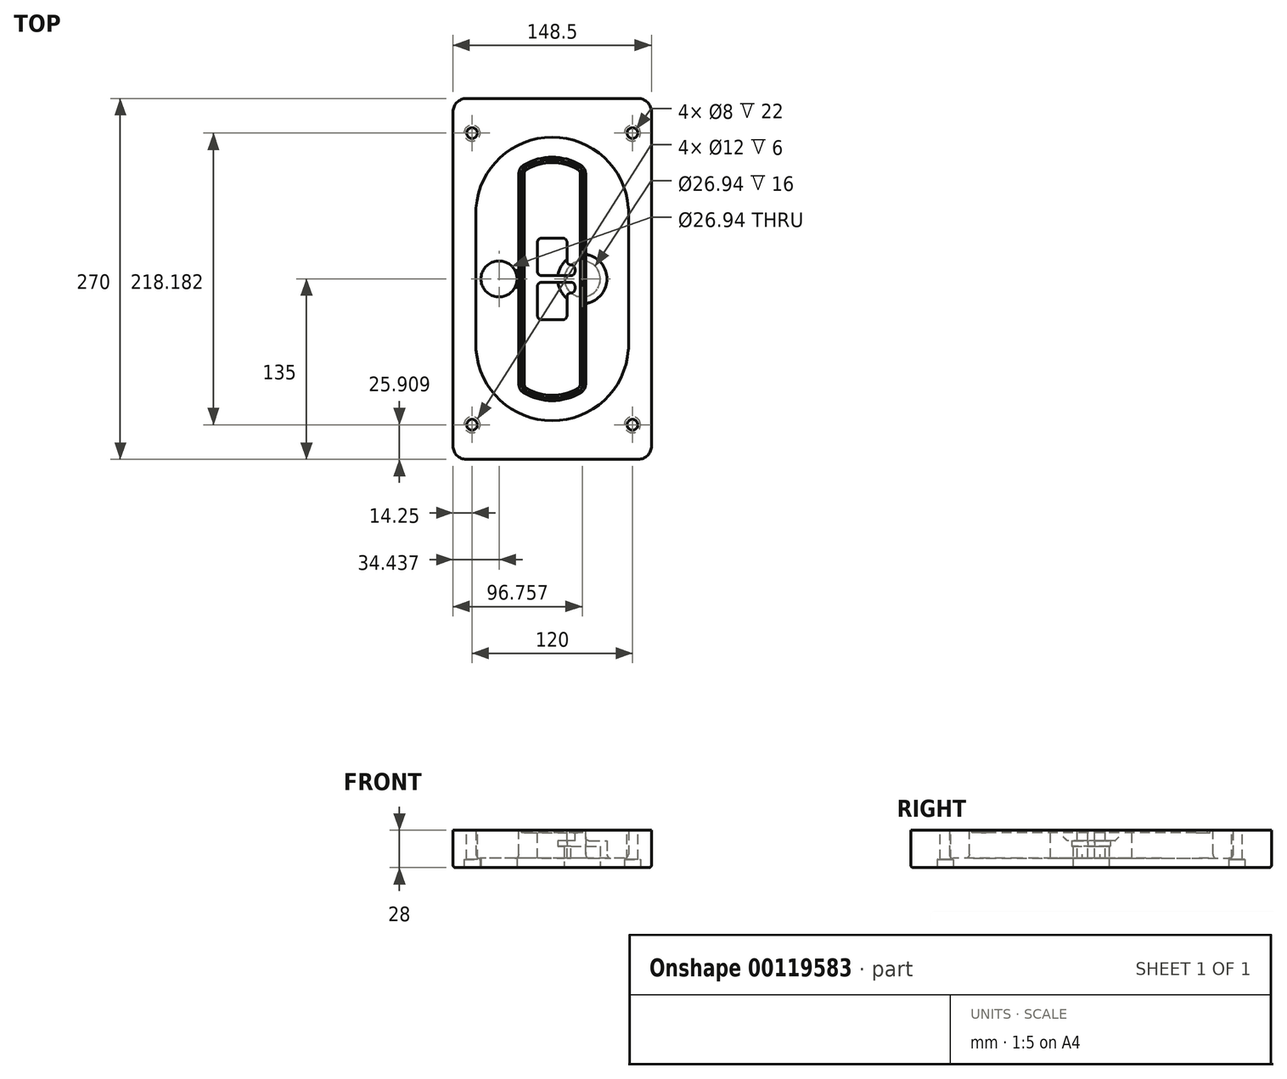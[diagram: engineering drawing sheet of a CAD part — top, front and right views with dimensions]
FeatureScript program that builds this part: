
annotation { "Feature Type Name" : "Feature", "Feature Type Description" : "" }
export const myFeature = defineFeature(function(context is Context, id is Id, definition is map)
    precondition{}
    {
        {
            var Q0;
            Q0=qCreatedBy(makeId("Top.planeOp"),FACE);
            var sketch = newSketch(context, id + "F0", { "sketchPlane" : qUnion([Q0])});
            skPoint(sketch, "E0.rect.middle", {"position": v(0, 0) * mm});
            skLineSegment(sketch, "E1.bottom", {"start": v(-64.25, -135) * mm, "end": v(64.25, -135) * mm});
            skLineSegment(sketch, "E1.top", {"start": v(-64.25, 135) * mm, "end": v(64.25, 135) * mm});
            skLineSegment(sketch, "E1.left", {"start": v(-74.25, -125) * mm, "end": v(-74.25, 125) * mm});
            skLineSegment(sketch, "E1.right", {"start": v(74.25, -125) * mm, "end": v(74.25, 125) * mm});
            skLineSegment(sketch, "E2", {"start": v(-74.25, 135) * mm, "end": v(74.25, -135) * mm, "construction": true});
            skLineSegment(sketch, "E3", {"start": v(74.25, 135) * mm, "end": v(-74.25, -135) * mm, "construction": true});
            skCircle(sketch, "E4", {"center": v(-60, 109.1) * mm, "radius": 4 * mm});
            skCircle(sketch, "E5", {"center": v(60, 109.1) * mm, "radius": 4 * mm});
            skCircle(sketch, "E6", {"center": v(60, -109.1) * mm, "radius": 4 * mm});
            skCircle(sketch, "E7", {"center": v(-60, -109.1) * mm, "radius": 4 * mm});
            skLineSegment(sketch, "E8", {"start": v(-60, 109.1) * mm, "end": v(60, 109.1) * mm, "construction": true});
            skLineSegment(sketch, "E9", {"start": v(60, 109.1) * mm, "end": v(60, -109.1) * mm, "construction": true});
            skLineSegment(sketch, "E10", {"start": v(60, -109.1) * mm, "end": v(-60, -109.1) * mm, "construction": true});
            skLineSegment(sketch, "E11", {"start": v(-60, -109.1) * mm, "end": v(-60, 109.1) * mm, "construction": true});
            skLineSegment(sketch, "E12", {"start": v(-60, 52.58) * mm, "end": v(-60, -52.58) * mm});
            skLineSegment(sketch, "E13", {"start": v(60, 52.58) * mm, "end": v(60, -52.58) * mm});
            skArc(sketch, "E14", {"start": v(59.97, 53.3) * mm, "mid": v(0, 109.1) * mm, "end": v(-59.97, 53.3) * mm});
            skArc(sketch, "E15", {"start": v(-59.97, -53.3) * mm, "mid": v(0, -109.1) * mm, "end": v(59.97, -53.3) * mm});
            skLineSegment(sketch, "E16", {"start": v(-60, 0) * mm, "end": v(60, 0) * mm, "construction": true});
            skPoint(sketch, "E17.visualSharp", {"position": v(-60, -45) * mm});
            skArc(sketch, "E17.filletArc", {"start": v(-60, -52.58) * mm, "mid": v(-60, -52.94) * mm, "end": v(-59.97, -53.3) * mm});
            skPoint(sketch, "E18.visualSharp", {"position": v(-60, 45) * mm});
            skArc(sketch, "E18.filletArc", {"start": v(-59.97, 53.3) * mm, "mid": v(-60, 52.94) * mm, "end": v(-60, 52.58) * mm});
            skPoint(sketch, "E19.visualSharp", {"position": v(60, 45) * mm});
            skArc(sketch, "E19.filletArc", {"start": v(60, 52.58) * mm, "mid": v(60, 52.94) * mm, "end": v(59.97, 53.3) * mm});
            skPoint(sketch, "E20.visualSharp", {"position": v(60, -45) * mm});
            skArc(sketch, "E20.filletArc", {"start": v(59.97, -53.3) * mm, "mid": v(60, -52.94) * mm, "end": v(60, -52.58) * mm});
            skPoint(sketch, "E21.visualSharp", {"position": v(-74.25, 135) * mm});
            skArc(sketch, "E21.filletArc", {"start": v(-64.25, 135) * mm, "mid": v(-71.32, 132.07) * mm, "end": v(-74.25, 125) * mm});
            skPoint(sketch, "E22.visualSharp", {"position": v(74.25, 135) * mm});
            skArc(sketch, "E22.filletArc", {"start": v(74.25, 125) * mm, "mid": v(71.32, 132.07) * mm, "end": v(64.25, 135) * mm});
            skPoint(sketch, "E23.visualSharp", {"position": v(74.25, -135) * mm});
            skArc(sketch, "E23.filletArc", {"start": v(64.25, -135) * mm, "mid": v(71.32, -132.07) * mm, "end": v(74.25, -125) * mm});
            skPoint(sketch, "E24.visualSharp", {"position": v(-74.25, -135) * mm});
            skArc(sketch, "E24.filletArc", {"start": v(-74.25, -125) * mm, "mid": v(-71.32, -132.07) * mm, "end": v(-64.25, -135) * mm});
            skArc(sketch, "E25.0", {"start": v(57, 52.58) * mm, "mid": v(57, 52.83) * mm, "end": v(56.98, 53.08) * mm});
            skLineSegment(sketch, "E25.1", {"start": v(57, 52.58) * mm, "end": v(57, -52.58) * mm});
            skArc(sketch, "E25.2", {"start": v(56.98, -53.08) * mm, "mid": v(57, -52.83) * mm, "end": v(57, -52.58) * mm});
            skArc(sketch, "E25.3", {"start": v(-56.98, -53.08) * mm, "mid": v(0, -106.1) * mm, "end": v(56.98, -53.08) * mm});
            skArc(sketch, "E25.4", {"start": v(-57, -52.58) * mm, "mid": v(-57, -52.83) * mm, "end": v(-56.98, -53.08) * mm});
            skArc(sketch, "E25.5", {"start": v(56.98, 53.08) * mm, "mid": v(0, 106.1) * mm, "end": v(-56.98, 53.08) * mm});
            skLineSegment(sketch, "E25.6", {"start": v(-57, 52.58) * mm, "end": v(-57, -52.58) * mm});
            skArc(sketch, "E25.7", {"start": v(-56.98, 53.08) * mm, "mid": v(-57, 52.83) * mm, "end": v(-57, 52.58) * mm});
            skArc(sketch, "E26.0", {"start": v(-63.96, 53.59) * mm, "mid": v(-64, 53.08) * mm, "end": v(-64, 52.58) * mm});
            skArc(sketch, "E26.1", {"start": v(63.96, 53.59) * mm, "mid": v(0, 113.1) * mm, "end": v(-63.96, 53.59) * mm});
            skArc(sketch, "E26.2", {"start": v(64, 52.58) * mm, "mid": v(64, 53.08) * mm, "end": v(63.96, 53.59) * mm});
            skLineSegment(sketch, "E26.3", {"start": v(64, 52.58) * mm, "end": v(64, -52.58) * mm});
            skArc(sketch, "E26.4", {"start": v(63.96, -53.59) * mm, "mid": v(64, -53.08) * mm, "end": v(64, -52.58) * mm});
            skLineSegment(sketch, "E26.5", {"start": v(-64, 52.58) * mm, "end": v(-64, -52.58) * mm});
            skArc(sketch, "E26.6", {"start": v(-63.96, -53.59) * mm, "mid": v(0, -113.1) * mm, "end": v(63.96, -53.59) * mm});
            skArc(sketch, "E26.7", {"start": v(-64, -52.58) * mm, "mid": v(-64, -53.08) * mm, "end": v(-63.96, -53.59) * mm});
            skSolve(sketch);
        }
        {
            var Q0;
            Q0=makeQuery(id+"F0.imprint","IMPRINT",FACE,{"disambiguationData":[TD([[makeQuery(id+"F0.imprint","IMPRINT",EDGE,{"derivedFrom":sQuery(id+"F0.wireOp",EDGE,"E1.bottom")}),1.0]])]});
            var Q1;
            Q1=makeQuery(id+"F0.imprint","IMPRINT",FACE,{"disambiguationData":[TD([[makeQuery(id+"F0.imprint","IMPRINT",EDGE,{"derivedFrom":sQuery(id+"F0.wireOp",EDGE,"E12")}),1.0]])]});
            var Q2;
            Q2=makeQuery(id+"F0.imprint","IMPRINT",FACE,{"disambiguationData":[TD([[makeQuery(id+"F0.imprint","IMPRINT",EDGE,{"derivedFrom":sQuery(id+"F0.wireOp",EDGE,"E25.0")}),1.0]])]});
            var Q3;
            Q3=makeQuery(id+"F0.imprint","IMPRINT",FACE,{"disambiguationData":[TD([[makeQuery(id+"F0.imprint","IMPRINT",EDGE,{"derivedFrom":sQuery(id+"F0.wireOp",EDGE,"E12")}),-1.0]])]});
            extrude(context, id + "F1", {"entities" : qUnion([Q0, Q1, Q2, Q3]), "oppositeDirection" : true, "depth" : 25 * mm});
        }
        {
            var Q0;
            Q0=makeQuery(id+"F0.imprint","IMPRINT",FACE,{"disambiguationData":[TD([[makeQuery(id+"F0.imprint","IMPRINT",EDGE,{"derivedFrom":sQuery(id+"F0.wireOp",EDGE,"E12")}),1.0]])]});
            extrude(context, id + "F2", {"entities" : qUnion([Q0]), "operationType" : NewBodyOperationType.ADD, "depth" : 3 * mm});
        }
        {
            var Q0;
            Q0=makeQuery(id+"F0.imprint","IMPRINT",FACE,{"disambiguationData":[TD([[makeQuery(id+"F0.imprint","IMPRINT",EDGE,{"derivedFrom":sQuery(id+"F0.wireOp",EDGE,"E25.0")}),1.0]])]});
            extrude(context, id + "F3", {"entities" : qUnion([Q0]), "operationType" : NewBodyOperationType.REMOVE, "oppositeDirection" : true, "depth" : 18 * mm});
        }
        {
            var Q0;
            Q0=makeQuery(id+"F2.opExtrude","CAP_FACE",FACE,{"disambiguationData":[OSD([sQuery(id+"F0.wireOp",EDGE,"E12"),sQuery(id+"F0.wireOp",EDGE,"E13"),sQuery(id+"F0.wireOp",EDGE,"E14"),sQuery(id+"F0.wireOp",EDGE,"E15"),sQuery(id+"F0.wireOp",EDGE,"E17.filletArc"),sQuery(id+"F0.wireOp",EDGE,"E18.filletArc"),sQuery(id+"F0.wireOp",EDGE,"E19.filletArc"),sQuery(id+"F0.wireOp",EDGE,"E20.filletArc"),sQuery(id+"F0.wireOp",EDGE,"E25.0"),sQuery(id+"F0.wireOp",EDGE,"E25.1"),sQuery(id+"F0.wireOp",EDGE,"E25.2"),sQuery(id+"F0.wireOp",EDGE,"E25.3"),sQuery(id+"F0.wireOp",EDGE,"E25.4"),sQuery(id+"F0.wireOp",EDGE,"E25.5"),sQuery(id+"F0.wireOp",EDGE,"E25.6"),sQuery(id+"F0.wireOp",EDGE,"E25.7")])],"isStart":false});
            var sketch = newSketch(context, id + "F4", { "sketchPlane" : qUnion([Q0])});
            skArc(sketch, "E27.0", {"start": v(-20.98, -85.5) * mm, "mid": v(0, -91.1) * mm, "end": v(20.98, -85.5) * mm});
            skArc(sketch, "E28.0", {"start": v(20.98, 85.5) * mm, "mid": v(0, 91.1) * mm, "end": v(-20.98, 85.5) * mm});
            skLineSegment(sketch, "E29", {"start": v(-25, 78.56) * mm, "end": v(-25, -78.56) * mm});
            skLineSegment(sketch, "E30", {"start": v(25, 78.56) * mm, "end": v(25, -78.56) * mm});
            skLineSegment(sketch, "E31", {"start": v(-25, 82.87) * mm, "end": v(25, 82.87) * mm, "construction": true});
            skLineSegment(sketch, "E32", {"start": v(-25, -82.87) * mm, "end": v(25, -82.87) * mm, "construction": true});
            skPoint(sketch, "E33.visualSharp", {"position": v(-25, 82.87) * mm});
            skArc(sketch, "E33.filletArc", {"start": v(-20.98, 85.5) * mm, "mid": v(-23.92, 82.56) * mm, "end": v(-25, 78.56) * mm});
            skPoint(sketch, "E34.visualSharp", {"position": v(25, 82.87) * mm});
            skArc(sketch, "E34.filletArc", {"start": v(25, 78.56) * mm, "mid": v(23.92, 82.56) * mm, "end": v(20.98, 85.5) * mm});
            skPoint(sketch, "E35.visualSharp", {"position": v(25, -82.87) * mm});
            skArc(sketch, "E35.filletArc", {"start": v(20.98, -85.5) * mm, "mid": v(23.92, -82.56) * mm, "end": v(25, -78.56) * mm});
            skPoint(sketch, "E36.visualSharp", {"position": v(-25, -82.87) * mm});
            skArc(sketch, "E36.filletArc", {"start": v(-25, -78.56) * mm, "mid": v(-23.92, -82.56) * mm, "end": v(-20.98, -85.5) * mm});
            skArc(sketch, "E37.0", {"start": v(56.98, 53.08) * mm, "mid": v(0, 106.1) * mm, "end": v(-56.98, 53.08) * mm});
            skArc(sketch, "E37.1", {"start": v(-56.98, 53.08) * mm, "mid": v(-57, 52.83) * mm, "end": v(-57, 52.58) * mm});
            skLineSegment(sketch, "E37.2", {"start": v(-57, 52.58) * mm, "end": v(-57, -52.58) * mm});
            skArc(sketch, "E37.3", {"start": v(-57, -52.58) * mm, "mid": v(-57, -52.83) * mm, "end": v(-56.98, -53.08) * mm});
            skArc(sketch, "E37.4", {"start": v(-56.98, -53.08) * mm, "mid": v(0, -106.1) * mm, "end": v(56.98, -53.08) * mm});
            skArc(sketch, "E37.5", {"start": v(56.98, -53.08) * mm, "mid": v(57, -52.83) * mm, "end": v(57, -52.58) * mm});
            skLineSegment(sketch, "E37.6", {"start": v(57, 52.58) * mm, "end": v(57, -52.58) * mm});
            skArc(sketch, "E37.7", {"start": v(57, 52.58) * mm, "mid": v(57, 52.83) * mm, "end": v(56.98, 53.08) * mm});
            skLineSegment(sketch, "E38.0", {"start": v(23, 78.56) * mm, "end": v(23, -78.56) * mm});
            skArc(sketch, "E38.1", {"start": v(19.99, -83.76) * mm, "mid": v(22.2, -81.56) * mm, "end": v(23, -78.56) * mm});
            skArc(sketch, "E38.2", {"start": v(-19.99, -83.76) * mm, "mid": v(0, -89.1) * mm, "end": v(19.99, -83.76) * mm});
            skArc(sketch, "E38.3", {"start": v(-23, -78.56) * mm, "mid": v(-22.2, -81.56) * mm, "end": v(-19.99, -83.76) * mm});
            skLineSegment(sketch, "E38.4", {"start": v(-23, 78.56) * mm, "end": v(-23, -78.56) * mm});
            skArc(sketch, "E38.5", {"start": v(23, 78.56) * mm, "mid": v(22.2, 81.56) * mm, "end": v(19.99, 83.76) * mm});
            skArc(sketch, "E38.6", {"start": v(-19.99, 83.76) * mm, "mid": v(-22.2, 81.56) * mm, "end": v(-23, 78.56) * mm});
            skArc(sketch, "E38.7", {"start": v(19.99, 83.76) * mm, "mid": v(0, 89.1) * mm, "end": v(-19.99, 83.76) * mm});
            skArc(sketch, "E39.0", {"start": v(21, 78.56) * mm, "mid": v(20.46, 80.56) * mm, "end": v(19, 82.02) * mm});
            skLineSegment(sketch, "E39.1", {"start": v(21, 78.56) * mm, "end": v(21, -78.56) * mm});
            skArc(sketch, "E39.2", {"start": v(19, -82.02) * mm, "mid": v(20.46, -80.56) * mm, "end": v(21, -78.56) * mm});
            skArc(sketch, "E39.3", {"start": v(-19, -82.02) * mm, "mid": v(0, -87.1) * mm, "end": v(19, -82.02) * mm});
            skArc(sketch, "E39.4", {"start": v(-21, -78.56) * mm, "mid": v(-20.46, -80.56) * mm, "end": v(-19, -82.02) * mm});
            skArc(sketch, "E39.5", {"start": v(19, 82.02) * mm, "mid": v(0, 87.1) * mm, "end": v(-19, 82.02) * mm});
            skLineSegment(sketch, "E39.6", {"start": v(-21, 78.56) * mm, "end": v(-21, -78.56) * mm});
            skArc(sketch, "E39.7", {"start": v(-19, 82.02) * mm, "mid": v(-20.46, 80.56) * mm, "end": v(-21, 78.56) * mm});
            skLineSegment(sketch, "E40", {"start": v(-25, 0) * mm, "end": v(25, 0) * mm, "construction": true});
            skLineSegment(sketch, "E41", {"start": v(-11, 5.5) * mm, "end": v(-11, 27.5) * mm});
            skLineSegment(sketch, "E42", {"start": v(-8, 30.5) * mm, "end": v(8, 30.5) * mm});
            skLineSegment(sketch, "E43", {"start": v(11, 27.5) * mm, "end": v(11, 13.5) * mm});
            skLineSegment(sketch, "E44", {"start": v(14, 10.5) * mm, "end": v(14, 10.5) * mm});
            skLineSegment(sketch, "E45", {"start": v(17, 7.5) * mm, "end": v(17, 5.5) * mm});
            skLineSegment(sketch, "E46", {"start": v(14, 2.5) * mm, "end": v(-8, 2.5) * mm});
            skPoint(sketch, "E47.visualSharp", {"position": v(-11, 30.5) * mm});
            skArc(sketch, "E47.filletArc", {"start": v(-8, 30.5) * mm, "mid": v(-10.12, 29.62) * mm, "end": v(-11, 27.5) * mm});
            skPoint(sketch, "E48.visualSharp", {"position": v(11, 30.5) * mm});
            skArc(sketch, "E48.filletArc", {"start": v(11, 27.5) * mm, "mid": v(10.12, 29.62) * mm, "end": v(8, 30.5) * mm});
            skPoint(sketch, "E49.visualSharp", {"position": v(11, 10.5) * mm});
            skArc(sketch, "E49.filletArc", {"start": v(11, 13.5) * mm, "mid": v(11.88, 11.38) * mm, "end": v(14, 10.5) * mm});
            skPoint(sketch, "E50.visualSharp", {"position": v(17, 10.5) * mm});
            skArc(sketch, "E50.filletArc", {"start": v(17, 7.5) * mm, "mid": v(16.12, 9.62) * mm, "end": v(14, 10.5) * mm});
            skPoint(sketch, "E51.visualSharp", {"position": v(17, 2.5) * mm});
            skArc(sketch, "E51.filletArc", {"start": v(14, 2.5) * mm, "mid": v(16.12, 3.38) * mm, "end": v(17, 5.5) * mm});
            skPoint(sketch, "E52.visualSharp", {"position": v(-11, 2.5) * mm});
            skArc(sketch, "E52.filletArc", {"start": v(-11, 5.5) * mm, "mid": v(-10.12, 3.38) * mm, "end": v(-8, 2.5) * mm});
            skLineSegment(sketch, "E53.0.MirrorCS", {"start": v(14, -2.5) * mm, "end": v(-8, -2.5) * mm});
            skArc(sketch, "E54.0.MirrorCS", {"start": v(-11, -5.5) * mm, "mid": v(-10.12, -3.38) * mm, "end": v(-8, -2.5) * mm});
            skLineSegment(sketch, "E55.0.MirrorCS", {"start": v(-11, -5.5) * mm, "end": v(-11, -27.5) * mm});
            skArc(sketch, "E56.0.MirrorCS", {"start": v(-8, -30.5) * mm, "mid": v(-10.12, -29.62) * mm, "end": v(-11, -27.5) * mm});
            skLineSegment(sketch, "E57.0.MirrorCS", {"start": v(-8, -30.5) * mm, "end": v(8, -30.5) * mm});
            skArc(sketch, "E58.0.MirrorCS", {"start": v(11, -27.5) * mm, "mid": v(10.12, -29.62) * mm, "end": v(8, -30.5) * mm});
            skLineSegment(sketch, "E59.0.MirrorCS", {"start": v(11, -27.5) * mm, "end": v(11, -13.5) * mm});
            skArc(sketch, "E60.0.MirrorCS", {"start": v(11, -13.5) * mm, "mid": v(11.88, -11.38) * mm, "end": v(14, -10.5) * mm});
            skArc(sketch, "E61.0.MirrorCS", {"start": v(17, -7.5) * mm, "mid": v(16.12, -9.62) * mm, "end": v(14, -10.5) * mm});
            skLineSegment(sketch, "E62.0.MirrorCS", {"start": v(17, -7.5) * mm, "end": v(17, -5.5) * mm});
            skArc(sketch, "E63.0.MirrorCS", {"start": v(14, -2.5) * mm, "mid": v(16.12, -3.38) * mm, "end": v(17, -5.5) * mm});
            skSolve(sketch);
        }
        {
            var Q0;
            Q0=makeQuery(id+"F4.imprint","IMPRINT",FACE,{"disambiguationData":[TD([[makeQuery(id+"F4.imprint","IMPRINT",EDGE,{"derivedFrom":sQuery(id+"F4.wireOp",EDGE,"E27.0")}),1.0]])]});
            var Q1;
            Q1=makeQuery(id+"F4.imprint","IMPRINT",FACE,{"disambiguationData":[TD([[makeQuery(id+"F4.imprint","IMPRINT",EDGE,{"derivedFrom":sQuery(id+"F4.wireOp",EDGE,"E38.0")}),-1.0]])]});
            var Q2;
            Q2=makeQuery(id+"F4.imprint","IMPRINT",FACE,{"disambiguationData":[TD([[makeQuery(id+"F4.imprint","IMPRINT",EDGE,{"derivedFrom":sQuery(id+"F4.wireOp",EDGE,"E39.0")}),1.0]])]});
            extrude(context, id + "F5", {"entities" : qUnion([Q0, Q1, Q2]), "operationType" : NewBodyOperationType.ADD, "endBound" : BoundingType.UP_TO_NEXT, "oppositeDirection" : true, "depth" : 25 * mm});
        }
        {
            var Q0;
            Q0=makeQuery(id+"F4.imprint","IMPRINT",FACE,{"disambiguationData":[TD([[makeQuery(id+"F4.imprint","IMPRINT",EDGE,{"derivedFrom":sQuery(id+"F4.wireOp",EDGE,"E38.0")}),-1.0]])]});
            extrude(context, id + "F6", {"entities" : qUnion([Q0]), "operationType" : NewBodyOperationType.REMOVE, "oppositeDirection" : true, "depth" : 2 * mm});
        }
        {
            var Q0;
            Q0=makeQuery(id+"F1.opExtrude","CAP_FACE",FACE,{"disambiguationData":[OSD([sQuery(id+"F0.wireOp",EDGE,"E1.bottom"),sQuery(id+"F0.wireOp",EDGE,"E1.top"),sQuery(id+"F0.wireOp",EDGE,"E1.left"),sQuery(id+"F0.wireOp",EDGE,"E1.right"),sQuery(id+"F0.wireOp",EDGE,"E4"),sQuery(id+"F0.wireOp",EDGE,"E5"),sQuery(id+"F0.wireOp",EDGE,"E6"),sQuery(id+"F0.wireOp",EDGE,"E7"),sQuery(id+"F0.wireOp",EDGE,"E21.filletArc"),sQuery(id+"F0.wireOp",EDGE,"E22.filletArc"),sQuery(id+"F0.wireOp",EDGE,"E23.filletArc"),sQuery(id+"F0.wireOp",EDGE,"E24.filletArc")])],"isStart":false});
            var sketch = newSketch(context, id + "F7", { "sketchPlane" : qUnion([Q0])});
            skCircle(sketch, "E64", {"center": v(22.5, 0) * mm, "radius": 13.47 * mm});
            skCircle(sketch, "E65", {"center": v(-39.81, 0) * mm, "radius": 13.47 * mm});
            skLineSegment(sketch, "E66", {"start": v(74.25, 0) * mm, "end": v(-74.25, 0) * mm});
            skCircle(sketch, "E67", {"center": v(22.5, 0) * mm, "radius": 18.47 * mm});
            skCircle(sketch, "E68", {"center": v(60, -109.1) * mm, "radius": 6 * mm});
            skCircle(sketch, "E69", {"center": v(-60, -109.1) * mm, "radius": 6 * mm});
            skCircle(sketch, "E70", {"center": v(-60, 109.1) * mm, "radius": 6 * mm});
            skCircle(sketch, "E71", {"center": v(60, 109.1) * mm, "radius": 6 * mm});
            skSolve(sketch);
        }
        {
            var Q0;
            {var subQ1=sQuery(id+"F7.wireOp",EDGE,"E66");var subQ4=sQuery(id+"F7.wireOp",EDGE,"E64");var subQ6=makeQuery(id+"F7.imprint","INTERSECT",VERTEX,{"disambiguationData":[OD(0.0)],"derivedFrom":[subQ4,subQ1]});Q0=makeQuery(id+"F7.imprint","IMPRINT",FACE,{"disambiguationData":[TD([[makeQuery(id+"F7.imprint","IMPRINT",EDGE,{"disambiguationData":[TD([[subQ6,-1.0]])],"derivedFrom":subQ4}),-1.0]])]});}
            var Q1;
            {var subQ0=sQuery(id+"F7.wireOp",EDGE,"E66");var subQ1=sQuery(id+"F7.wireOp",EDGE,"E64");var subQ3=makeQuery(id+"F7.imprint","INTERSECT",VERTEX,{"disambiguationData":[OD(0.0)],"derivedFrom":[subQ1,subQ0]});Q1=makeQuery(id+"F7.imprint","IMPRINT",FACE,{"disambiguationData":[TD([[makeQuery(id+"F7.imprint","IMPRINT",EDGE,{"disambiguationData":[TD([[subQ3,-1.0]])],"derivedFrom":subQ1}),1.0]])]});}
            var Q2;
            {var subQ0=sQuery(id+"F7.wireOp",EDGE,"E66");var subQ1=sQuery(id+"F7.wireOp",EDGE,"E64");var subQ3=makeQuery(id+"F7.imprint","INTERSECT",VERTEX,{"disambiguationData":[OD(0.0)],"derivedFrom":[subQ1,subQ0]});Q2=makeQuery(id+"F7.imprint","IMPRINT",FACE,{"disambiguationData":[TD([[makeQuery(id+"F7.imprint","IMPRINT",EDGE,{"disambiguationData":[TD([[subQ3,1.0]])],"derivedFrom":subQ1}),1.0]])]});}
            var Q3;
            {var subQ1=sQuery(id+"F7.wireOp",EDGE,"E66");var subQ4=sQuery(id+"F7.wireOp",EDGE,"E64");var subQ6=makeQuery(id+"F7.imprint","INTERSECT",VERTEX,{"disambiguationData":[OD(0.0)],"derivedFrom":[subQ4,subQ1]});Q3=makeQuery(id+"F7.imprint","IMPRINT",FACE,{"disambiguationData":[TD([[makeQuery(id+"F7.imprint","IMPRINT",EDGE,{"disambiguationData":[TD([[subQ6,1.0]])],"derivedFrom":subQ4}),-1.0]])]});}
            extrude(context, id + "F8", {"entities" : qUnion([Q0, Q1, Q2, Q3]), "operationType" : NewBodyOperationType.ADD, "oppositeDirection" : true, "depth" : 20 * mm});
        }
        {
            var Q0;
            {var subQ0=sQuery(id+"F7.wireOp",EDGE,"E66");var subQ1=sQuery(id+"F7.wireOp",EDGE,"E64");var subQ3=makeQuery(id+"F7.imprint","INTERSECT",VERTEX,{"disambiguationData":[OD(0.0)],"derivedFrom":[subQ1,subQ0]});Q0=makeQuery(id+"F7.imprint","IMPRINT",FACE,{"disambiguationData":[TD([[makeQuery(id+"F7.imprint","IMPRINT",EDGE,{"disambiguationData":[TD([[subQ3,-1.0]])],"derivedFrom":subQ1}),1.0]])]});}
            var Q1;
            {var subQ0=sQuery(id+"F7.wireOp",EDGE,"E66");var subQ1=sQuery(id+"F7.wireOp",EDGE,"E64");var subQ3=makeQuery(id+"F7.imprint","INTERSECT",VERTEX,{"disambiguationData":[OD(0.0)],"derivedFrom":[subQ1,subQ0]});Q1=makeQuery(id+"F7.imprint","IMPRINT",FACE,{"disambiguationData":[TD([[makeQuery(id+"F7.imprint","IMPRINT",EDGE,{"disambiguationData":[TD([[subQ3,1.0]])],"derivedFrom":subQ1}),1.0]])]});}
            extrude(context, id + "F9", {"entities" : qUnion([Q0, Q1]), "operationType" : NewBodyOperationType.REMOVE, "oppositeDirection" : true, "depth" : 16 * mm});
        }
        {
            var Q0;
            {var subQ0=sQuery(id+"F7.wireOp",EDGE,"E66");var subQ1=sQuery(id+"F7.wireOp",EDGE,"E65");var subQ3=makeQuery(id+"F7.imprint","INTERSECT",VERTEX,{"disambiguationData":[OD(0.0)],"derivedFrom":[subQ1,subQ0]});Q0=makeQuery(id+"F7.imprint","IMPRINT",FACE,{"disambiguationData":[TD([[makeQuery(id+"F7.imprint","IMPRINT",EDGE,{"disambiguationData":[TD([[subQ3,-1.0]])],"derivedFrom":subQ1}),1.0]])]});}
            var Q1;
            {var subQ0=sQuery(id+"F7.wireOp",EDGE,"E66");var subQ1=sQuery(id+"F7.wireOp",EDGE,"E65");var subQ3=makeQuery(id+"F7.imprint","INTERSECT",VERTEX,{"disambiguationData":[OD(0.0)],"derivedFrom":[subQ1,subQ0]});Q1=makeQuery(id+"F7.imprint","IMPRINT",FACE,{"disambiguationData":[TD([[makeQuery(id+"F7.imprint","IMPRINT",EDGE,{"disambiguationData":[TD([[subQ3,1.0]])],"derivedFrom":subQ1}),1.0]])]});}
            extrude(context, id + "F10", {"entities" : qUnion([Q0, Q1]), "operationType" : NewBodyOperationType.REMOVE, "oppositeDirection" : true, "depth" : 25 * mm});
        }
        {
            var Q0;
            Q0=makeQuery(id+"F7.imprint","IMPRINT",FACE,{"disambiguationData":[TD([[makeQuery(id+"F7.imprint","IMPRINT",EDGE,{"derivedFrom":sQuery(id+"F7.wireOp",EDGE,"E68")}),1.0]])]});
            var Q1;
            Q1=makeQuery(id+"F7.imprint","IMPRINT",FACE,{"disambiguationData":[TD([[makeQuery(id+"F7.imprint","IMPRINT",EDGE,{"derivedFrom":makeQuery(id+"F1.opExtrude","CAP_EDGE",EDGE,{"disambiguationData":[OSD([sQuery(id+"F0.wireOp",EDGE,"E5")])],"isStart":false})}),-1.0]])]});
            var Q2;
            Q2=makeQuery(id+"F7.imprint","IMPRINT",FACE,{"disambiguationData":[TD([[makeQuery(id+"F7.imprint","IMPRINT",EDGE,{"derivedFrom":sQuery(id+"F7.wireOp",EDGE,"E69")}),1.0]])]});
            var Q3;
            Q3=makeQuery(id+"F7.imprint","IMPRINT",FACE,{"disambiguationData":[TD([[makeQuery(id+"F7.imprint","IMPRINT",EDGE,{"derivedFrom":makeQuery(id+"F1.opExtrude","CAP_EDGE",EDGE,{"disambiguationData":[OSD([sQuery(id+"F0.wireOp",EDGE,"E4")])],"isStart":false})}),-1.0]])]});
            var Q4;
            Q4=makeQuery(id+"F7.imprint","IMPRINT",FACE,{"disambiguationData":[TD([[makeQuery(id+"F7.imprint","IMPRINT",EDGE,{"derivedFrom":sQuery(id+"F7.wireOp",EDGE,"E70")}),1.0]])]});
            var Q5;
            Q5=makeQuery(id+"F7.imprint","IMPRINT",FACE,{"disambiguationData":[TD([[makeQuery(id+"F7.imprint","IMPRINT",EDGE,{"derivedFrom":makeQuery(id+"F1.opExtrude","CAP_EDGE",EDGE,{"disambiguationData":[OSD([sQuery(id+"F0.wireOp",EDGE,"E7")])],"isStart":false})}),-1.0]])]});
            var Q6;
            Q6=makeQuery(id+"F7.imprint","IMPRINT",FACE,{"disambiguationData":[TD([[makeQuery(id+"F7.imprint","IMPRINT",EDGE,{"derivedFrom":sQuery(id+"F7.wireOp",EDGE,"E71")}),1.0]])]});
            var Q7;
            Q7=makeQuery(id+"F7.imprint","IMPRINT",FACE,{"disambiguationData":[TD([[makeQuery(id+"F7.imprint","IMPRINT",EDGE,{"derivedFrom":makeQuery(id+"F1.opExtrude","CAP_EDGE",EDGE,{"disambiguationData":[OSD([sQuery(id+"F0.wireOp",EDGE,"E6")])],"isStart":false})}),-1.0]])]});
            extrude(context, id + "F11", {"entities" : qUnion([Q0, Q1, Q2, Q3, Q4, Q5, Q6, Q7]), "operationType" : NewBodyOperationType.REMOVE, "oppositeDirection" : true, "depth" : 6 * mm});
        }
        {
            var Q0;
            Q0=makeQuery(id+"F9.boolean.opBoolean","COPY",FACE,{"derivedFrom":makeQuery(id+"F9.opExtrude","CAP_FACE",FACE,{"disambiguationData":[OSD([sQuery(id+"F7.wireOp",EDGE,"E64")])],"isStart":false})});
            var sketch = newSketch(context, id + "F12", { "sketchPlane" : qUnion([Q0])});
            skArc(sketch, "E72.0", {"start": v(11, 14.45) * mm, "mid": v(6.45, 9.13) * mm, "end": v(4.2, 2.5) * mm});
            skArc(sketch, "E72.1", {"start": v(4.2, -2.5) * mm, "mid": v(6.45, -9.13) * mm, "end": v(11, -14.45) * mm});
            skLineSegment(sketch, "E73", {"start": v(4.2, -2.5) * mm, "end": v(14, -2.5) * mm});
            skLineSegment(sketch, "E74.0", {"start": v(14, 2.5) * mm, "end": v(4.2, 2.5) * mm});
            skArc(sketch, "E74.1", {"start": v(14, 2.5) * mm, "mid": v(16.12, 3.38) * mm, "end": v(17, 5.5) * mm});
            skLineSegment(sketch, "E74.2", {"start": v(17, 7.5) * mm, "end": v(17, 5.5) * mm});
            skArc(sketch, "E74.3", {"start": v(17, 7.5) * mm, "mid": v(16.12, 9.62) * mm, "end": v(14, 10.5) * mm});
            skArc(sketch, "E74.4", {"start": v(11, 13.5) * mm, "mid": v(11.88, 11.38) * mm, "end": v(14, 10.5) * mm});
            skLineSegment(sketch, "E74.5", {"start": v(11, 14.45) * mm, "end": v(11, 13.5) * mm});
            skLineSegment(sketch, "E74.7", {"start": v(14, -2.5) * mm, "end": v(4.2, -2.5) * mm});
            skArc(sketch, "E74.8", {"start": v(14, -2.5) * mm, "mid": v(16.12, -3.38) * mm, "end": v(17, -5.5) * mm});
            skLineSegment(sketch, "E74.9", {"start": v(17, -7.5) * mm, "end": v(17, -5.5) * mm});
            skArc(sketch, "E74.10", {"start": v(17, -7.5) * mm, "mid": v(16.12, -9.62) * mm, "end": v(14, -10.5) * mm});
            skArc(sketch, "E74.11", {"start": v(11, -13.5) * mm, "mid": v(11.88, -11.38) * mm, "end": v(14, -10.5) * mm});
            skLineSegment(sketch, "E74.12", {"start": v(11, -14.45) * mm, "end": v(11, -13.5) * mm});
            skPoint(sketch, "E75.orphan", {"position": v(11, -27.5) * mm});
            skPoint(sketch, "E76.orphan", {"position": v(-8, -2.5) * mm});
            skPoint(sketch, "E77.orphan", {"position": v(-8, 2.5) * mm});
            skPoint(sketch, "E78.orphan", {"position": v(11, 27.5) * mm});
            skSolve(sketch);
        }
        {
            var Q0;
            {var subQ7=sQuery(id+"F12.wireOp",EDGE,"E72.0");var subQ14=sQuery(id+"F12.wireOp",EDGE,"E72.1");var subQ16=sQuery(id+"F12.wireOp",EDGE,"E74.1");var subQ18=sQuery(id+"F12.wireOp",EDGE,"E74.8");Q0=qUnion([makeQuery(id+"F12.imprint","IMPRINT",FACE,{"disambiguationData":[TD([[makeQuery(id+"F12.imprint","IMPRINT",EDGE,{"derivedFrom":subQ7}),1.0]])]}),makeQuery(id+"F12.imprint","IMPRINT",FACE,{"disambiguationData":[TD([[makeQuery(id+"F12.imprint","IMPRINT",EDGE,{"derivedFrom":subQ14}),1.0]])]}),makeQuery(id+"F12.imprint","IMPRINT",FACE,{"disambiguationData":[TD([[makeQuery(id+"F12.imprint","IMPRINT",EDGE,{"derivedFrom":subQ16}),1.0]])]}),makeQuery(id+"F12.imprint","IMPRINT",FACE,{"disambiguationData":[TD([[makeQuery(id+"F12.imprint","IMPRINT",EDGE,{"derivedFrom":subQ18}),-1.0]])]})]);}
            var Q1;
            Q1=makeQuery(id+"F5.boolean.opBoolean","SPLIT",FACE,{"disambiguationData":[TD([makeQuery(id+"F5.opExtrude","SWEPT_FACE",FACE,{"disambiguationData":[OSD([sQuery(id+"F4.wireOp",EDGE,"E41")])]})])],"derivedFrom":makeQuery(id+"F3.boolean.opBoolean","COPY",FACE,{"derivedFrom":makeQuery(id+"F3.opExtrude","CAP_FACE",FACE,{"disambiguationData":[OSD([sQuery(id+"F0.wireOp",EDGE,"E25.0"),sQuery(id+"F0.wireOp",EDGE,"E25.1"),sQuery(id+"F0.wireOp",EDGE,"E25.2"),sQuery(id+"F0.wireOp",EDGE,"E25.3"),sQuery(id+"F0.wireOp",EDGE,"E25.4"),sQuery(id+"F0.wireOp",EDGE,"E25.5"),sQuery(id+"F0.wireOp",EDGE,"E25.6"),sQuery(id+"F0.wireOp",EDGE,"E25.7")])],"isStart":false})})});
            extrude(context, id + "F13", {"entities" : qUnion([Q0]), "operationType" : NewBodyOperationType.REMOVE, "endBound" : BoundingType.UP_TO_SURFACE, "endBoundEntityFace" : qUnion([Q1]), "depth" : 25 * mm});
        }
        {
            var Q0;
            Q0=makeQuery(id+"F3.boolean.opBoolean","COPY",EDGE,{"derivedFrom":makeQuery(id+"F3.opExtrude","CAP_EDGE",EDGE,{"disambiguationData":[OSD([sQuery(id+"F0.wireOp",EDGE,"E25.6")])],"isStart":false})});
            var Q1;
            Q1=makeQuery(id+"F8.boolean.opBoolean","INTERSECT",EDGE,{"derivedFrom":[makeQuery(id+"F5.opExtrude","SWEPT_FACE",FACE,{"disambiguationData":[OSD([sQuery(id+"F4.wireOp",EDGE,"E30")])]}),makeQuery(id+"F8.opExtrude","CAP_FACE",FACE,{"disambiguationData":[OSD([sQuery(id+"F7.wireOp",EDGE,"E67")])],"isStart":false})]});
            var Q2;
            Q2=makeQuery(id+"F8.boolean.opBoolean","INTERSECT",EDGE,{"disambiguationData":[OD(1.0)],"derivedFrom":[makeQuery(id+"F5.opExtrude","SWEPT_FACE",FACE,{"disambiguationData":[OSD([sQuery(id+"F4.wireOp",EDGE,"E30")])]}),makeQuery(id+"F8.opExtrude","SWEPT_FACE",FACE,{"disambiguationData":[OSD([sQuery(id+"F7.wireOp",EDGE,"E67")])]})]});
            var Q3;
            {var subQ0=sQuery(id+"F4.wireOp",EDGE,"E30");Q3=makeQuery(id+"F8.boolean.opBoolean","SPLIT",EDGE,{"disambiguationData":[TD([makeQuery(id+"F5.opExtrude","SWEPT_FACE",FACE,{"disambiguationData":[OSD([sQuery(id+"F4.wireOp",EDGE,"E35.filletArc")])]})])],"derivedFrom":makeQuery(id+"F5.opExtrude","CAP_EDGE",EDGE,{"disambiguationData":[OSD([subQ0])],"isStart":false})});}
            var Q4;
            {var subQ0=sQuery(id+"F0.wireOp",EDGE,"E25.7");var subQ1=sQuery(id+"F0.wireOp",EDGE,"E25.1");var subQ2=sQuery(id+"F0.wireOp",EDGE,"E25.6");var subQ3=sQuery(id+"F0.wireOp",EDGE,"E25.5");var subQ4=sQuery(id+"F0.wireOp",EDGE,"E25.4");var subQ5=sQuery(id+"F0.wireOp",EDGE,"E25.0");var subQ6=sQuery(id+"F0.wireOp",EDGE,"E25.2");var subQ7=sQuery(id+"F0.wireOp",EDGE,"E25.3");Q4=makeQuery(id+"F8.boolean.opBoolean","INTERSECT",EDGE,{"derivedFrom":[makeQuery(id+"F5.boolean.opBoolean","SPLIT",FACE,{"disambiguationData":[TD([makeQuery(id+"F2.opExtrude","SWEPT_FACE",FACE,{"disambiguationData":[OSD([subQ5])]})])],"derivedFrom":makeQuery(id+"F3.boolean.opBoolean","COPY",FACE,{"derivedFrom":makeQuery(id+"F3.opExtrude","CAP_FACE",FACE,{"disambiguationData":[OSD([subQ5,subQ1,subQ6,subQ7,subQ4,subQ3,subQ2,subQ0])],"isStart":false})})}),makeQuery(id+"F8.opExtrude","SWEPT_FACE",FACE,{"disambiguationData":[OSD([sQuery(id+"F7.wireOp",EDGE,"E67")])]})]});}
            var Q5;
            Q5=makeQuery(id+"F8.boolean.opBoolean","INTERSECT",EDGE,{"disambiguationData":[OD(0.0)],"derivedFrom":[makeQuery(id+"F5.opExtrude","SWEPT_FACE",FACE,{"disambiguationData":[OSD([sQuery(id+"F4.wireOp",EDGE,"E30")])]}),makeQuery(id+"F8.opExtrude","SWEPT_FACE",FACE,{"disambiguationData":[OSD([sQuery(id+"F7.wireOp",EDGE,"E67")])]})]});
            fillet(context, id + "F14", {"entities" : qUnion([Q0, Q1, Q2, Q3, Q4, Q5]), "radius" : 3 * mm, "tangentPropagation" : true, "allowEdgeOverflow" : false});
        }
        {
            var Q0;
            Q0=makeQuery(id+"F1.opExtrude","CAP_EDGE",EDGE,{"disambiguationData":[OSD([sQuery(id+"F0.wireOp",EDGE,"E1.bottom")])],"isStart":false});
            fillet(context, id + "F15", {"entities" : qUnion([Q0]), "radius" : 2 * mm, "tangentPropagation" : true, "allowEdgeOverflow" : false});
        }
        {
            var Q0;
            {var subQ0=sQuery(id+"F0.wireOp",EDGE,"E22.filletArc");var subQ1=sQuery(id+"F0.wireOp",EDGE,"E7");var subQ2=sQuery(id+"F0.wireOp",EDGE,"E6");var subQ3=sQuery(id+"F0.wireOp",EDGE,"E5");var subQ4=sQuery(id+"F0.wireOp",EDGE,"E4");var subQ5=sQuery(id+"F0.wireOp",EDGE,"E1.bottom");var subQ6=sQuery(id+"F0.wireOp",EDGE,"E21.filletArc");var subQ7=sQuery(id+"F0.wireOp",EDGE,"E1.top");var subQ8=sQuery(id+"F0.wireOp",EDGE,"E1.left");var subQ9=sQuery(id+"F0.wireOp",EDGE,"E1.right");var subQ10=sQuery(id+"F0.wireOp",EDGE,"E23.filletArc");var subQ11=sQuery(id+"F0.wireOp",EDGE,"E24.filletArc");Q0=makeQuery(id+"F2.boolean.opBoolean","SPLIT",FACE,{"disambiguationData":[TD([makeQuery(id+"F1.opExtrude","SWEPT_FACE",FACE,{"disambiguationData":[OSD([subQ5])]})])],"derivedFrom":makeQuery(id+"F1.opExtrude","CAP_FACE",FACE,{"disambiguationData":[OSD([subQ5,subQ7,subQ8,subQ9,subQ4,subQ3,subQ2,subQ1,subQ6,subQ0,subQ10,subQ11])],"isStart":true})});}
            var sketch = newSketch(context, id + "F16", { "sketchPlane" : qUnion([Q0])});
            skCircle(sketch, "E79", {"center": v(0, 165) * mm, "radius": 6 * mm});
            skPoint(sketch, "E79.centerSnap0", {"position": v(0, 135) * mm});
            skLineSegment(sketch, "E80", {"start": v(0, 165) * mm, "end": v(0, 135) * mm, "construction": true});
            skLineSegment(sketch, "E81", {"start": v(-33, 135) * mm, "end": v(33, 135) * mm});
            skLineSegment(sketch, "E82", {"start": v(-33, 135) * mm, "end": v(-15, 153) * mm});
            skLineSegment(sketch, "E83", {"start": v(33, 135) * mm, "end": v(15, 153) * mm});
            skLineSegment(sketch, "E84", {"start": v(15, 153) * mm, "end": v(15, 165) * mm});
            skLineSegment(sketch, "E85", {"start": v(-15, 165) * mm, "end": v(-15, 153) * mm});
            skArc(sketch, "E86", {"start": v(15, 165) * mm, "mid": v(0, 180) * mm, "end": v(-15, 165) * mm});
            skLineSegment(sketch, "E87", {"start": v(-74.25, 0) * mm, "end": v(74.25, 0) * mm, "construction": true});
            skLineSegment(sketch, "E88.MirrorCS", {"start": v(15, 165) * mm, "end": v(15, 153) * mm});
            skLineSegment(sketch, "E89.MirrorCS", {"start": v(-15, 153) * mm, "end": v(-15, 165) * mm});
            skArc(sketch, "E90.MirrorCS", {"start": v(-15, 165) * mm, "mid": v(0, 180) * mm, "end": v(15, 165) * mm});
            skLineSegment(sketch, "E91.MirrorCS", {"start": v(33, 135) * mm, "end": v(-33, 135) * mm});
            skLineSegment(sketch, "E92.MirrorCS", {"start": v(74.25, 0) * mm, "end": v(-74.25, 0) * mm, "construction": true});
            skLineSegment(sketch, "E93.MirrorCS", {"start": v(-15, -165) * mm, "end": v(-15, -153) * mm});
            skLineSegment(sketch, "E94.MirrorCS", {"start": v(-15, -153) * mm, "end": v(-15, -165) * mm});
            skLineSegment(sketch, "E95.MirrorCS", {"start": v(15, -165) * mm, "end": v(15, -153) * mm});
            skLineSegment(sketch, "E96.MirrorCS", {"start": v(15, -153) * mm, "end": v(15, -165) * mm});
            skLineSegment(sketch, "E97.MirrorCS", {"start": v(33, -135) * mm, "end": v(15, -153) * mm});
            skLineSegment(sketch, "E98.MirrorCS", {"start": v(-33, -135) * mm, "end": v(33, -135) * mm});
            skLineSegment(sketch, "E99.MirrorCS", {"start": v(-33, -135) * mm, "end": v(-15, -153) * mm});
            skCircle(sketch, "E100.MirrorC", {"center": v(0, -165) * mm, "radius": 6 * mm});
            skLineSegment(sketch, "E101.MirrorCS", {"start": v(33, -135) * mm, "end": v(-33, -135) * mm});
            skArc(sketch, "E102.MirrorCS", {"start": v(15, -165) * mm, "mid": v(0, -180) * mm, "end": v(-15, -165) * mm});
            skPoint(sketch, "E103.MirrorP", {"position": v(0, -135) * mm});
            skArc(sketch, "E104.MirrorCS", {"start": v(-15, -165) * mm, "mid": v(0, -180) * mm, "end": v(15, -165) * mm});
            skLineSegment(sketch, "E105.MirrorCS", {"start": v(0, -165) * mm, "end": v(0, -135) * mm, "construction": true});
            skSolve(sketch);
        }
        {
            var Q0;
            {var subQ4=sQuery(id+"F16.wireOp",EDGE,"E81");Q0=makeQuery(id+"F16.imprint","IMPRINT",FACE,{"disambiguationData":[TD([[makeQuery(id+"F16.imprint","IMPRINT",EDGE,{"derivedFrom":subQ4}),-1.0]])]});}
            var Q1;
            Q1=makeQuery(id+"F16.imprint","IMPRINT",FACE,{"disambiguationData":[TD([[makeQuery(id+"F16.imprint","IMPRINT",EDGE,{"derivedFrom":sQuery(id+"F16.wireOp",EDGE,"E88.MirrorCS")}),-1.0]])]});
            var Q2;
            Q2=makeQuery(id+"F16.imprint","IMPRINT",FACE,{"disambiguationData":[TD([[makeQuery(id+"F16.imprint","IMPRINT",EDGE,{"derivedFrom":sQuery(id+"F16.wireOp",EDGE,"E94.MirrorCS")}),1.0]])]});
            var Q3;
            Q3=makeQuery(id+"F2.opExtrude","CAP_FACE",FACE,{"disambiguationData":[OSD([sQuery(id+"F0.wireOp",EDGE,"E12"),sQuery(id+"F0.wireOp",EDGE,"E13"),sQuery(id+"F0.wireOp",EDGE,"E14"),sQuery(id+"F0.wireOp",EDGE,"E15"),sQuery(id+"F0.wireOp",EDGE,"E17.filletArc"),sQuery(id+"F0.wireOp",EDGE,"E18.filletArc"),sQuery(id+"F0.wireOp",EDGE,"E19.filletArc"),sQuery(id+"F0.wireOp",EDGE,"E20.filletArc"),sQuery(id+"F0.wireOp",EDGE,"E25.0"),sQuery(id+"F0.wireOp",EDGE,"E25.1"),sQuery(id+"F0.wireOp",EDGE,"E25.2"),sQuery(id+"F0.wireOp",EDGE,"E25.3"),sQuery(id+"F0.wireOp",EDGE,"E25.4"),sQuery(id+"F0.wireOp",EDGE,"E25.5"),sQuery(id+"F0.wireOp",EDGE,"E25.6"),sQuery(id+"F0.wireOp",EDGE,"E25.7")])],"isStart":false});
            extrude(context, id + "F17", {"entities" : qUnion([Q0, Q1, Q2]), "operationType" : NewBodyOperationType.ADD, "endBound" : BoundingType.UP_TO_SURFACE, "endBoundEntityFace" : qUnion([Q3]), "depth" : 25 * mm});
        }
    });
